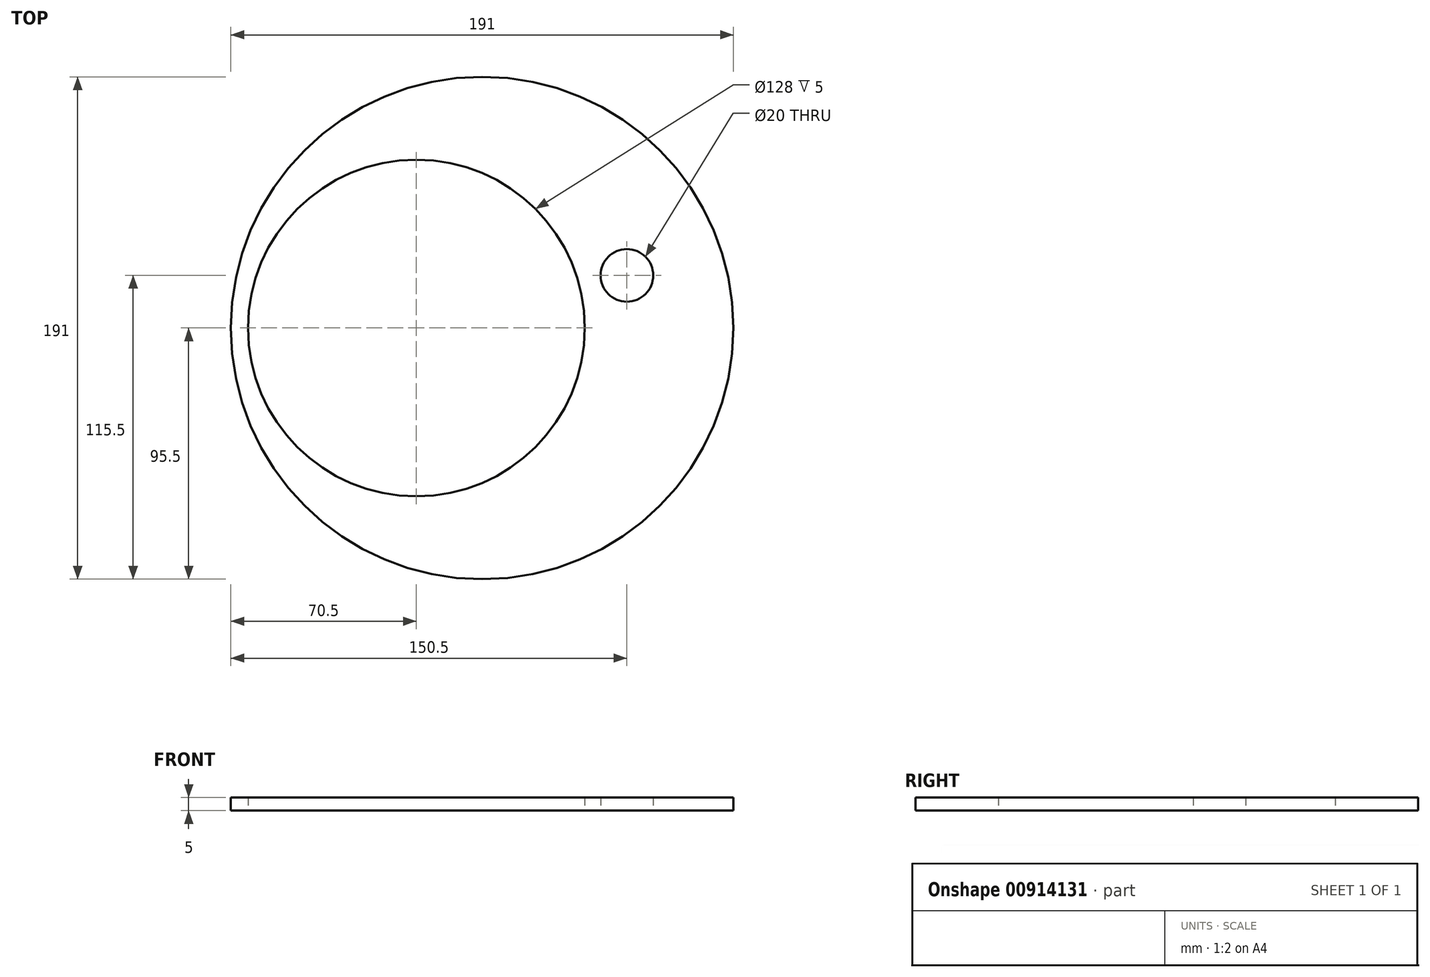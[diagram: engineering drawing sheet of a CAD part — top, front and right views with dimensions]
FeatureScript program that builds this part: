
annotation { "Feature Type Name" : "Feature", "Feature Type Description" : "" }
export const myFeature = defineFeature(function(context is Context, id is Id, definition is map)
    precondition{}
    {
        {
            var Q0;
            Q0=qCreatedBy(makeId("Top.planeOp"),FACE);
            var sketch = newSketch(context, id + "F0", { "sketchPlane" : qUnion([Q0])});
            skCircle(sketch, "E0", {"center": v(0, 0) * mm, "radius": 95.5 * mm});
            skCircle(sketch, "E1", {"center": v(-25, 0) * mm, "radius": 64 * mm});
            skCircle(sketch, "E2", {"center": v(55, 20) * mm, "radius": 10 * mm});
            skSolve(sketch);
        }
        {
            var Q0;
            Q0=makeQuery(id+"F0.imprint","IMPRINT",FACE,{"disambiguationData":[TD([[makeQuery(id+"F0.imprint","IMPRINT",EDGE,{"derivedFrom":sQuery(id+"F0.wireOp",EDGE,"E0")}),1.0]])]});
            extrude(context, id + "F1", {"entities" : qUnion([Q0]), "depth" : 5 * mm, "offsetDistance" : 25 * mm});
        }
    });
